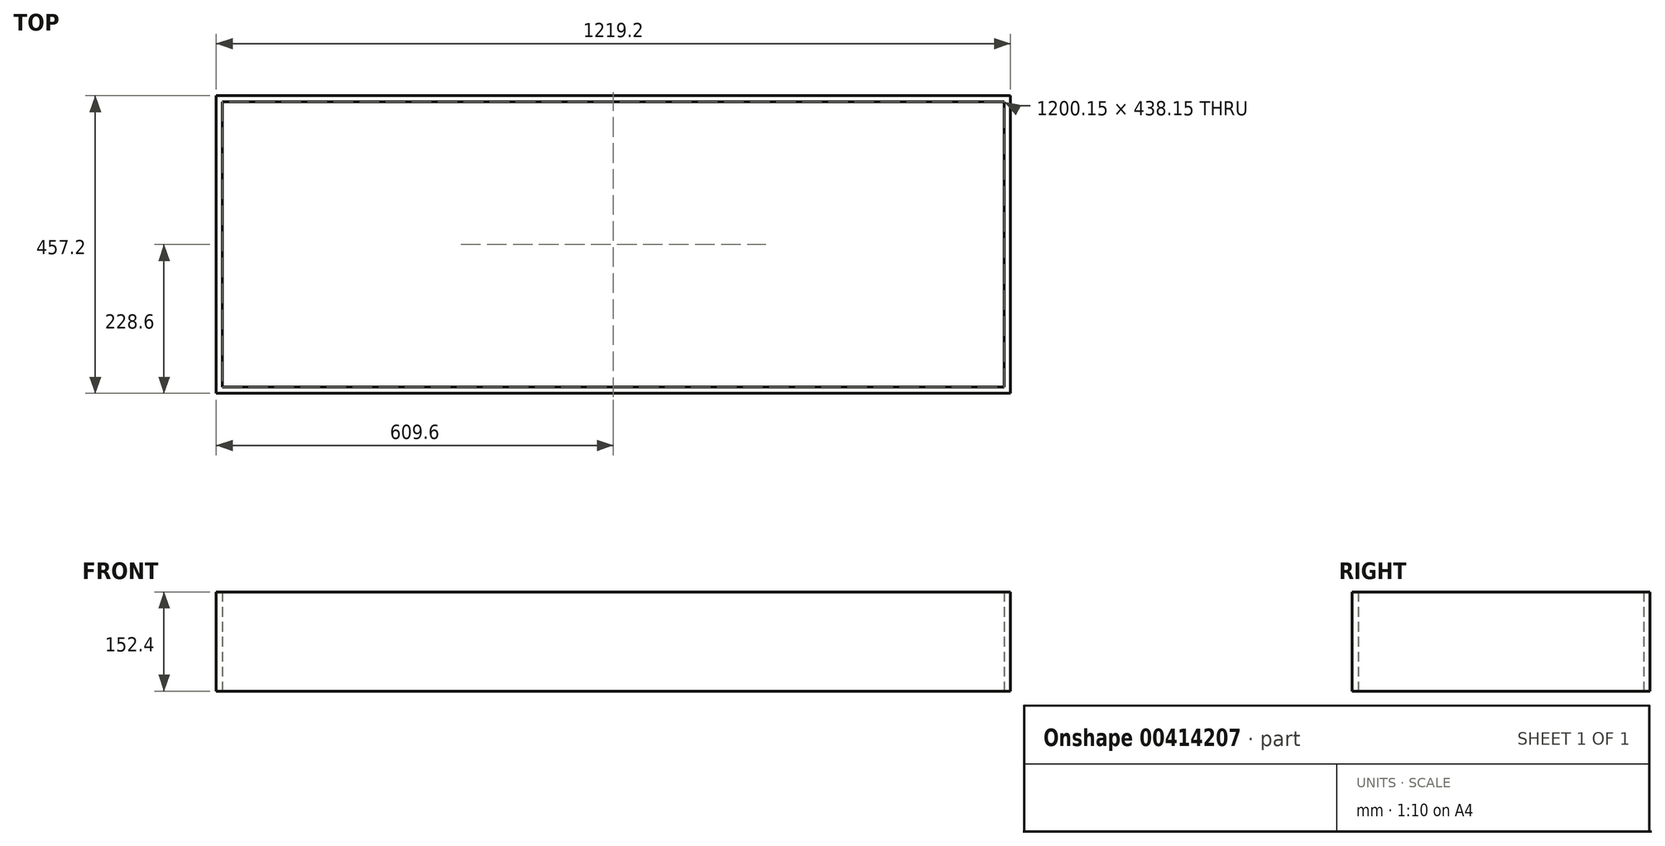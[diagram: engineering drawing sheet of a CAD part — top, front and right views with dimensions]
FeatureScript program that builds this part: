
annotation { "Feature Type Name" : "Feature", "Feature Type Description" : "" }
export const myFeature = defineFeature(function(context is Context, id is Id, definition is map)
    precondition{}
    {
        {
            var Q0;
            Q0=qCreatedBy(makeId("Top.planeOp"),FACE);
            var sketch = newSketch(context, id + "F0", { "sketchPlane" : qUnion([Q0])});
            skLineSegment(sketch, "E0.bottom", {"start": v(609.6, 228.6) * mm, "end": v(-609.6, 228.6) * mm});
            skLineSegment(sketch, "E0.top", {"start": v(609.6, -228.6) * mm, "end": v(-609.6, -228.6) * mm});
            skLineSegment(sketch, "E0.left", {"start": v(609.6, 228.6) * mm, "end": v(609.6, -228.6) * mm});
            skLineSegment(sketch, "E0.right", {"start": v(-609.6, 228.6) * mm, "end": v(-609.6, -228.6) * mm});
            skPoint(sketch, "E0.middle", {"position": v(0, 0) * mm});
            skLineSegment(sketch, "E1.bottom", {"start": v(600.08, -219.07) * mm, "end": v(-600.08, -219.08) * mm});
            skLineSegment(sketch, "E1.top", {"start": v(600.08, 219.08) * mm, "end": v(-600.08, 219.07) * mm});
            skLineSegment(sketch, "E1.left", {"start": v(600.08, -219.07) * mm, "end": v(600.08, 219.08) * mm});
            skLineSegment(sketch, "E1.right", {"start": v(-600.08, -219.08) * mm, "end": v(-600.08, 219.07) * mm});
            skSolve(sketch);
        }
        {
            var Q0;
            Q0 = qSketchRegion(id + "F0", true);
            extrude(context, id + "F1", {"entities" : qUnion([Q0]), "depth" : 152.4 * mm});
        }
    });
